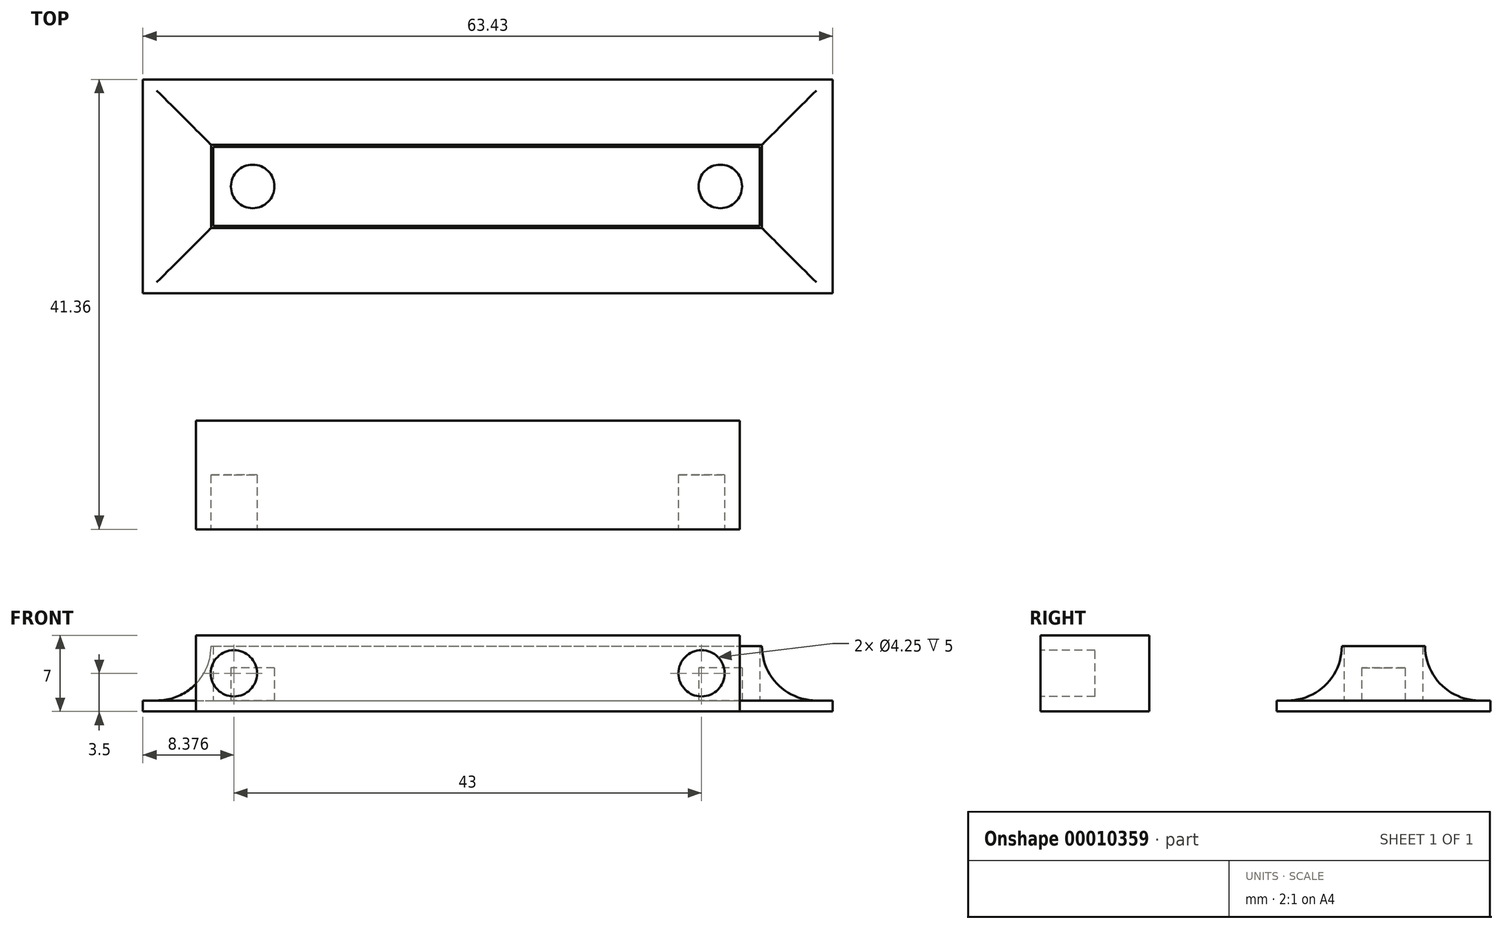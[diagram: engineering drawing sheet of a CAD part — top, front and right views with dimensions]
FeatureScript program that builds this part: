
annotation { "Feature Type Name" : "Feature", "Feature Type Description" : "" }
export const myFeature = defineFeature(function(context is Context, id is Id, definition is map)
    precondition{}
    {
        {
            var Q0;
            Q0=qCreatedBy(makeId("Top.planeOp"),FACE);
            var sketch = newSketch(context, id + "F0", { "sketchPlane" : qUnion([Q0])});
            skLineSegment(sketch, "E0.bottom", {"start": v(-46.4, 51.28) * mm, "end": v(17.02, 51.28) * mm});
            skLineSegment(sketch, "E0.top", {"start": v(-46.4, 31.63) * mm, "end": v(17.02, 31.63) * mm});
            skLineSegment(sketch, "E0.left", {"start": v(-46.4, 51.28) * mm, "end": v(-46.4, 31.63) * mm});
            skLineSegment(sketch, "E0.right", {"start": v(17.02, 51.28) * mm, "end": v(17.02, 31.63) * mm});
            skLineSegment(sketch, "E1.bottom", {"start": v(-39.93, 45.08) * mm, "end": v(10.32, 45.08) * mm});
            skLineSegment(sketch, "E1.top", {"start": v(-39.93, 37.83) * mm, "end": v(10.32, 37.83) * mm});
            skLineSegment(sketch, "E1.left", {"start": v(-39.93, 45.08) * mm, "end": v(-39.93, 37.83) * mm});
            skLineSegment(sketch, "E1.right", {"start": v(10.32, 45.08) * mm, "end": v(10.32, 37.83) * mm});
            skLineSegment(sketch, "E2", {"start": v(-39.93, 41.45) * mm, "end": v(-36.3, 41.45) * mm, "construction": true});
            skLineSegment(sketch, "E3", {"start": v(-36.3, 41.45) * mm, "end": v(-36.3, 45.08) * mm, "construction": true});
            skLineSegment(sketch, "E4", {"start": v(10.32, 41.45) * mm, "end": v(6.7, 41.45) * mm, "construction": true});
            skLineSegment(sketch, "E5", {"start": v(6.7, 41.45) * mm, "end": v(6.7, 45.08) * mm, "construction": true});
            skCircle(sketch, "E6", {"center": v(-36.3, 41.45) * mm, "radius": 2 * mm});
            skCircle(sketch, "E7", {"center": v(6.7, 41.45) * mm, "radius": 2 * mm});
            skLineSegment(sketch, "E8.0", {"start": v(10.52, 45.28) * mm, "end": v(10.52, 37.63) * mm});
            skLineSegment(sketch, "E8.1", {"start": v(-40.13, 45.28) * mm, "end": v(10.52, 45.28) * mm});
            skLineSegment(sketch, "E8.2", {"start": v(-40.13, 45.28) * mm, "end": v(-40.13, 37.63) * mm});
            skLineSegment(sketch, "E8.3", {"start": v(-40.13, 37.63) * mm, "end": v(10.52, 37.63) * mm});
            skLineSegment(sketch, "E9", {"start": v(10.52, 45.28) * mm, "end": v(10.52, 51.28) * mm, "construction": true});
            skLineSegment(sketch, "E10", {"start": v(10.52, 37.63) * mm, "end": v(10.52, 31.63) * mm, "construction": true});
            skSolve(sketch);
        }
        {
            var Q0;
            Q0=makeQuery(id+"F0.imprint","IMPRINT",FACE,{"disambiguationData":[TD([[makeQuery(id+"F0.imprint","IMPRINT",EDGE,{"derivedFrom":sQuery(id+"F0.wireOp",EDGE,"E1.bottom")}),1.0]])]});
            extrude(context, id + "F1", {"entities" : qUnion([Q0]), "depth" : 6 * mm});
        }
        {
            var Q0;
            Q0=makeQuery(id+"F0.imprint","IMPRINT",FACE,{"disambiguationData":[TD([[makeQuery(id+"F0.imprint","IMPRINT",EDGE,{"derivedFrom":sQuery(id+"F0.wireOp",EDGE,"E6")}),1.0]])]});
            var Q1;
            Q1=makeQuery(id+"F0.imprint","IMPRINT",FACE,{"disambiguationData":[TD([[makeQuery(id+"F0.imprint","IMPRINT",EDGE,{"derivedFrom":sQuery(id+"F0.wireOp",EDGE,"E7")}),1.0]])]});
            extrude(context, id + "F2", {"entities" : qUnion([Q0, Q1]), "depth" : 4 * mm});
        }
        {
            var Q0;
            Q0=makeQuery(id+"F0.imprint","IMPRINT",FACE,{"disambiguationData":[TD([[makeQuery(id+"F0.imprint","IMPRINT",EDGE,{"derivedFrom":sQuery(id+"F0.wireOp",EDGE,"E0.bottom")}),-1.0]])]});
            var Q1;
            Q1=makeQuery(id+"F0.imprint","IMPRINT",FACE,{"disambiguationData":[TD([[makeQuery(id+"F0.imprint","IMPRINT",EDGE,{"derivedFrom":sQuery(id+"F0.wireOp",EDGE,"E1.bottom")}),-1.0]])]});
            var Q2;
            Q2=makeQuery(id+"F0.imprint","IMPRINT",FACE,{"disambiguationData":[TD([[makeQuery(id+"F0.imprint","IMPRINT",EDGE,{"derivedFrom":sQuery(id+"F0.wireOp",EDGE,"E1.bottom")}),1.0]])]});
            var Q3;
            Q3=makeQuery(id+"F0.imprint","IMPRINT",FACE,{"disambiguationData":[TD([[makeQuery(id+"F0.imprint","IMPRINT",EDGE,{"derivedFrom":sQuery(id+"F0.wireOp",EDGE,"E7")}),1.0]])]});
            var Q4;
            Q4=makeQuery(id+"F0.imprint","IMPRINT",FACE,{"disambiguationData":[TD([[makeQuery(id+"F0.imprint","IMPRINT",EDGE,{"derivedFrom":sQuery(id+"F0.wireOp",EDGE,"E6")}),1.0]])]});
            extrude(context, id + "F3", {"entities" : qUnion([Q0, Q1, Q2, Q3, Q4]), "operationType" : NewBodyOperationType.ADD, "depth" : 1 * mm});
        }
        {
            var Q0;
            Q0=makeQuery(id+"F3.boolean.opBoolean","INTERSECT",EDGE,{"derivedFrom":[makeQuery(id+"F1.opExtrude","SWEPT_FACE",FACE,{"disambiguationData":[OSD([sQuery(id+"F0.wireOp",EDGE,"E8.0")])]}),makeQuery(id+"F3.opExtrude","CAP_FACE",FACE,{"disambiguationData":[OSD([sQuery(id+"F0.wireOp",EDGE,"E0.bottom"),sQuery(id+"F0.wireOp",EDGE,"E0.top"),sQuery(id+"F0.wireOp",EDGE,"E0.left"),sQuery(id+"F0.wireOp",EDGE,"E0.right")])],"isStart":false})]});
            var Q1;
            Q1=makeQuery(id+"F3.boolean.opBoolean","INTERSECT",EDGE,{"derivedFrom":[makeQuery(id+"F1.opExtrude","SWEPT_FACE",FACE,{"disambiguationData":[OSD([sQuery(id+"F0.wireOp",EDGE,"E8.1")])]}),makeQuery(id+"F3.opExtrude","CAP_FACE",FACE,{"disambiguationData":[OSD([sQuery(id+"F0.wireOp",EDGE,"E0.bottom"),sQuery(id+"F0.wireOp",EDGE,"E0.top"),sQuery(id+"F0.wireOp",EDGE,"E0.left"),sQuery(id+"F0.wireOp",EDGE,"E0.right")])],"isStart":false})]});
            var Q2;
            Q2=makeQuery(id+"F3.boolean.opBoolean","INTERSECT",EDGE,{"derivedFrom":[makeQuery(id+"F1.opExtrude","SWEPT_FACE",FACE,{"disambiguationData":[OSD([sQuery(id+"F0.wireOp",EDGE,"E8.3")])]}),makeQuery(id+"F3.opExtrude","CAP_FACE",FACE,{"disambiguationData":[OSD([sQuery(id+"F0.wireOp",EDGE,"E0.bottom"),sQuery(id+"F0.wireOp",EDGE,"E0.top"),sQuery(id+"F0.wireOp",EDGE,"E0.left"),sQuery(id+"F0.wireOp",EDGE,"E0.right")])],"isStart":false})]});
            var Q3;
            Q3=makeQuery(id+"F3.boolean.opBoolean","INTERSECT",EDGE,{"derivedFrom":[makeQuery(id+"F1.opExtrude","SWEPT_FACE",FACE,{"disambiguationData":[OSD([sQuery(id+"F0.wireOp",EDGE,"E8.2")])]}),makeQuery(id+"F3.opExtrude","CAP_FACE",FACE,{"disambiguationData":[OSD([sQuery(id+"F0.wireOp",EDGE,"E0.bottom"),sQuery(id+"F0.wireOp",EDGE,"E0.top"),sQuery(id+"F0.wireOp",EDGE,"E0.left"),sQuery(id+"F0.wireOp",EDGE,"E0.right")])],"isStart":false})]});
            fillet(context, id + "F4", {"entities" : qUnion([Q0, Q1, Q2, Q3]), "radius" : 5 * mm, "tangentPropagation" : true, "allowEdgeOverflow" : false});
        }
        {
            var Q0;
            Q0=qCreatedBy(makeId("Top.planeOp"),FACE);
            var sketch = newSketch(context, id + "F5", { "sketchPlane" : qUnion([Q0])});
            skLineSegment(sketch, "E11.0", {"start": v(-39.93, 45.08) * mm, "end": v(10.32, 45.08) * mm});
            skLineSegment(sketch, "E11.1", {"start": v(-39.93, 45.08) * mm, "end": v(-39.93, 37.83) * mm});
            skLineSegment(sketch, "E11.2", {"start": v(-39.93, 37.83) * mm, "end": v(10.32, 37.83) * mm});
            skLineSegment(sketch, "E11.3", {"start": v(10.32, 45.08) * mm, "end": v(10.32, 37.83) * mm});
            skCircle(sketch, "E12.0", {"center": v(-36.3, 41.45) * mm, "radius": 2 * mm});
            skCircle(sketch, "E12.1", {"center": v(6.7, 41.45) * mm, "radius": 2 * mm});
            skLineSegment(sketch, "E13.bottom", {"start": v(-41.53, 19.92) * mm, "end": v(8.47, 19.92) * mm});
            skLineSegment(sketch, "E13.top", {"start": v(-41.53, 9.92) * mm, "end": v(8.47, 9.92) * mm});
            skLineSegment(sketch, "E13.left", {"start": v(-41.53, 19.92) * mm, "end": v(-41.53, 9.92) * mm});
            skLineSegment(sketch, "E13.right", {"start": v(8.47, 19.92) * mm, "end": v(8.47, 9.92) * mm});
            skSolve(sketch);
        }
        {
            var Q0;
            Q0=makeQuery(id+"F5.imprint","IMPRINT",FACE,{"disambiguationData":[TD([[makeQuery(id+"F5.imprint","IMPRINT",EDGE,{"derivedFrom":sQuery(id+"F5.wireOp",EDGE,"E13.bottom")}),-1.0]])]});
            extrude(context, id + "F6", {"entities" : qUnion([Q0]), "depth" : 7 * mm});
        }
        {
            var Q0;
            Q0=makeQuery(id+"F6.opExtrude","SWEPT_FACE",FACE,{"disambiguationData":[OSD([sQuery(id+"F5.wireOp",EDGE,"E13.top")])]});
            var sketch = newSketch(context, id + "F7", { "sketchPlane" : qUnion([Q0])});
            skLineSegment(sketch, "E14", {"start": v(-41.53, 3.5) * mm, "end": v(-38.03, 3.5) * mm, "construction": true});
            skLineSegment(sketch, "E15", {"start": v(-38.03, 3.5) * mm, "end": v(-38.03, 7) * mm, "construction": true});
            skLineSegment(sketch, "E16", {"start": v(8.47, 3.5) * mm, "end": v(4.97, 3.5) * mm, "construction": true});
            skLineSegment(sketch, "E17", {"start": v(4.97, 3.5) * mm, "end": v(4.97, 7) * mm, "construction": true});
            skCircle(sketch, "E18", {"center": v(4.97, 3.5) * mm, "radius": 2.12 * mm});
            skCircle(sketch, "E19", {"center": v(-38.03, 3.5) * mm, "radius": 2.12 * mm});
            skSolve(sketch);
        }
        {
            var Q0;
            Q0=makeQuery(id+"F7.imprint","IMPRINT",FACE,{"disambiguationData":[TD([[makeQuery(id+"F7.imprint","IMPRINT",EDGE,{"derivedFrom":sQuery(id+"F7.wireOp",EDGE,"E19")}),1.0]])]});
            var Q1;
            Q1=makeQuery(id+"F7.imprint","IMPRINT",FACE,{"disambiguationData":[TD([[makeQuery(id+"F7.imprint","IMPRINT",EDGE,{"derivedFrom":sQuery(id+"F7.wireOp",EDGE,"E18")}),1.0]])]});
            extrude(context, id + "F8", {"entities" : qUnion([Q0, Q1]), "operationType" : NewBodyOperationType.REMOVE, "oppositeDirection" : true, "depth" : 5 * mm});
        }
    });
